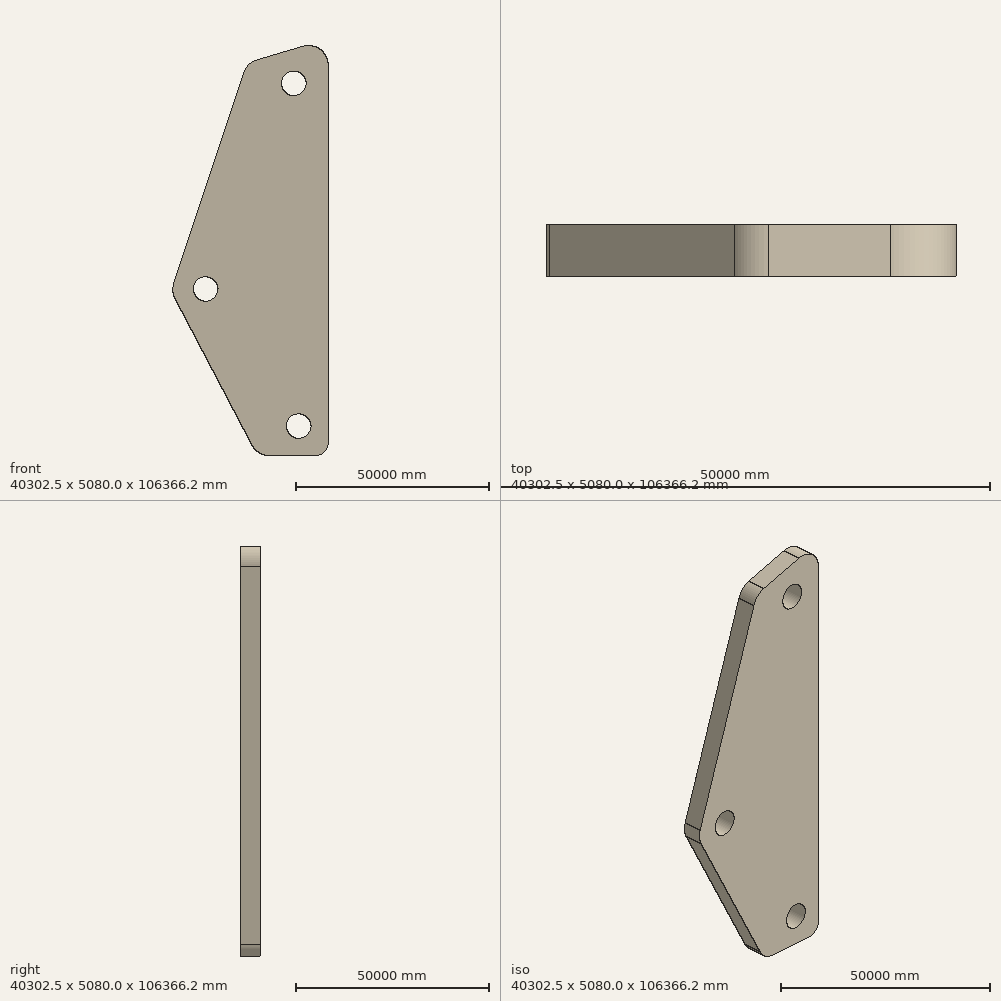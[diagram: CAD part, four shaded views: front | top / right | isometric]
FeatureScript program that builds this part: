
annotation { "Feature Type Name" : "Feature", "Feature Type Description" : "" }
export const myFeature = defineFeature(function(context is Context, id is Id, definition is map)
    precondition{}
    {
        {
            var Q0;
            Q0=qCreatedBy(makeId("Front.planeOp"),FACE);
            var sketch = newSketch(context, id + "F0", { "sketchPlane" : qUnion([Q0])});
            skLineSegment(sketch, "E0", {"start": v(5.06, -19.05) * mm, "end": v(11.18, -19.05) * mm});
            skLineSegment(sketch, "E1", {"start": v(12.7, -17.53) * mm, "end": v(12.7, 30.93) * mm});
            skPoint(sketch, "E2.visualSharp", {"position": v(12.7, -19.05) * mm});
            skArc(sketch, "E2.filletArc", {"start": v(11.18, -19.05) * mm, "mid": v(12.25, -18.6) * mm, "end": v(12.7, -17.53) * mm});
            skLineSegment(sketch, "E3", {"start": v(2.8, -17.7) * mm, "end": v(-7.16, 1.28) * mm});
            skLineSegment(sketch, "E4", {"start": v(-7.32, 3.27) * mm, "end": v(1.8, 30.62) * mm});
            skLineSegment(sketch, "E5", {"start": v(3.47, 32.25) * mm, "end": v(9.43, 34.03) * mm});
            skPoint(sketch, "E6.visualSharp", {"position": v(2.2, 31.87) * mm});
            skArc(sketch, "E6.filletArc", {"start": v(3.47, 32.25) * mm, "mid": v(2.43, 31.64) * mm, "end": v(1.8, 30.62) * mm});
            skLineSegment(sketch, "E7", {"start": v(12.7, 30.93) * mm, "end": v(12.7, 31.6) * mm});
            skArc(sketch, "E8.filletArc", {"start": v(12.7, 31.6) * mm, "mid": v(11.68, 33.63) * mm, "end": v(9.43, 34.03) * mm});
            skPoint(sketch, "E9.visualSharp", {"position": v(-7.66, 2.24) * mm});
            skArc(sketch, "E9.filletArc", {"start": v(-7.32, 3.27) * mm, "mid": v(-7.44, 2.26) * mm, "end": v(-7.16, 1.28) * mm});
            skPoint(sketch, "E10.visualSharp", {"position": v(3.52, -19.05) * mm});
            skArc(sketch, "E10.filletArc", {"start": v(2.8, -17.7) * mm, "mid": v(3.74, -18.68) * mm, "end": v(5.06, -19.05) * mm});
            skSolve(sketch);
        }
        {
            var Q0;
            Q0=makeQuery(id+"F0.imprint","IMPRINT",FACE,{"disambiguationData":[TD([[makeQuery(id+"F0.imprint","IMPRINT",EDGE,{"derivedFrom":sQuery(id+"F0.wireOp",EDGE,"E0")}),1.0]])]});
            extrude(context, id + "F1", {"entities" : qUnion([Q0]), "depth" : 2.54 * mm, "offsetDistance" : 25.4 * mm});
        }
        {
            var Q0;
            Q0=makeQuery(id+"F1.opExtrude","SWEPT_BODY",BODY,{"disambiguationData":[OSD([sQuery(id+"F0.wireOp",EDGE,"E0"),sQuery(id+"F0.wireOp",EDGE,"E1"),sQuery(id+"F0.wireOp",EDGE,"DfivezfX-YEGE-21nc-EM4w-vph0sAHb5fQF"),sQuery(id+"F0.wireOp",EDGE,"1c5ee6ff-9f80-4013-89b8-8fa25c837359.filletArc"),sQuery(id+"F0.wireOp",EDGE,"6896a488-95c1-4e29-957f-146f1feb13ec.filletArc"),sQuery(id+"F0.wireOp",EDGE,"E2.filletArc")])]});
            var Q1;
            Q1=makeQuery(id+"F1.opExtrude","CAP_VERTEX",VERTEX,{"disambiguationData":[OSD([sQuery(id+"F0.wireOp",EDGE,"E1"),sQuery(id+"F0.wireOp",EDGE,"1c5ee6ff-9f80-4013-89b8-8fa25c837359.filletArc")])],"isStart":false});
            transform(context, id + "F2", {"entities" : qUnion([Q0]), "transformType" : TransformType.SCALE_UNIFORMLY, "scale" : 2000, "scalePoint" : qUnion([Q1]), "makeCopy" : false});
        }
        {
            var Q0;
            Q0=makeQuery(id+"F1.opExtrude","CAP_FACE",FACE,{"disambiguationData":[OSD([sQuery(id+"F0.wireOp",EDGE,"E0"),sQuery(id+"F0.wireOp",EDGE,"E1"),sQuery(id+"F0.wireOp",EDGE,"DfivezfX-YEGE-21nc-EM4w-vph0sAHb5fQF"),sQuery(id+"F0.wireOp",EDGE,"1c5ee6ff-9f80-4013-89b8-8fa25c837359.filletArc"),sQuery(id+"F0.wireOp",EDGE,"6896a488-95c1-4e29-957f-146f1feb13ec.filletArc"),sQuery(id+"F0.wireOp",EDGE,"E2.filletArc")])],"isStart":false});
            cPlane(context, id + "F3", {"entities" : qUnion([Q0]), "cplaneType" : CPlaneType.OFFSET, "offset" : 25.4 * mm, "width" : 152.4 * mm, "height" : 152.4 * mm});
        }
        {
            var Q0;
            Q0=qCreatedBy(id+"F3.planeOp",FACE);
            var sketch = newSketch(context, id + "F4", { "sketchPlane" : qUnion([Q0])});
            skLineSegment(sketch, "E11.0.0", {"start": v(-6521.9, 103088) * mm, "end": v(-18438.7, 99526.65) * mm});
            skArc(sketch, "E11.0.1", {"start": v(-18438.7, 99526.65) * mm, "mid": v(-20519.67, 98307.12) * mm, "end": v(-21803.6, 96265.26) * mm});
            skLineSegment(sketch, "E11.0.2", {"start": v(-21803.6, 96265.26) * mm, "end": v(-40029.28, 41568.08) * mm});
            skArc(sketch, "E11.0.3", {"start": v(-40029.28, 41568.08) * mm, "mid": v(-40273.12, 39550.88) * mm, "end": v(-39706.92, 37599.48) * mm});
            skLineSegment(sketch, "E11.0.4", {"start": v(-39706.92, 37599.48) * mm, "end": v(-19770, -348.22) * mm});
            skArc(sketch, "E11.0.5", {"start": v(-19770, -348.22) * mm, "mid": v(-17900.05, -2333.45) * mm, "end": v(-15272.89, -3065.53) * mm});
            skLineSegment(sketch, "E11.0.6", {"start": v(-15272.89, -3065.53) * mm, "end": v(-3035.3, -3065.53) * mm});
            skArc(sketch, "E11.0.7", {"start": v(-3035.3, -3065.53) * mm, "mid": v(-880.04, -2172.79) * mm, "end": v(12.7, -17.53) * mm});
            skLineSegment(sketch, "E11.0.8", {"start": v(12.7, -17.53) * mm, "end": v(12.7, 98220.7) * mm});
            skArc(sketch, "E11.0.9", {"start": v(12.7, 98220.7) * mm, "mid": v(-2032.74, 102294.75) * mm, "end": v(-6521.9, 103088) * mm});
            skCircle(sketch, "E12", {"center": v(-7607.3, 4554.47) * mm, "radius": 3175 * mm});
            skCircle(sketch, "E13", {"center": v(-31737.3, 40114.47) * mm, "radius": 3175 * mm});
            skCircle(sketch, "E14", {"center": v(-8877.3, 93454.47) * mm, "radius": 3175 * mm});
            skSolve(sketch);
        }
        {
            var Q0;
            Q0=makeQuery(id+"F4.imprint","IMPRINT",FACE,{"disambiguationData":[TD([[makeQuery(id+"F4.imprint","IMPRINT",EDGE,{"derivedFrom":sQuery(id+"F4.wireOp",EDGE,"E14")}),1.0]])]});
            var Q1;
            Q1=makeQuery(id+"F4.imprint","IMPRINT",FACE,{"disambiguationData":[TD([[makeQuery(id+"F4.imprint","IMPRINT",EDGE,{"derivedFrom":sQuery(id+"F4.wireOp",EDGE,"E13")}),1.0]])]});
            var Q2;
            Q2=makeQuery(id+"F4.imprint","IMPRINT",FACE,{"disambiguationData":[TD([[makeQuery(id+"F4.imprint","IMPRINT",EDGE,{"derivedFrom":sQuery(id+"F4.wireOp",EDGE,"E12")}),1.0]])]});
            extrude(context, id + "F5", {"entities" : qUnion([Q0, Q1, Q2]), "operationType" : NewBodyOperationType.REMOVE, "endBound" : BoundingType.THROUGH_ALL, "oppositeDirection" : true, "depth" : 25.4 * mm, "offsetDistance" : 25.4 * mm});
        }
    });
